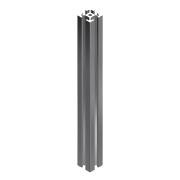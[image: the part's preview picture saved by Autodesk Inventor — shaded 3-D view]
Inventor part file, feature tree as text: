
AUTODESK INVENTOR PART (.ipt)
format: ipt  version: 2018 (Build 220112000, 112)  size: 148,480 bytes
history: native  units: mm
features: extrude x1, sketch x1
ambient origin geometry x8: Origin, YZ Plane, XZ Plane, XY Plane, X Axis, Y Axis, Z Axis, Center Point
bodies: Solid1 (feature_tree)
feature tree (2):
  extrude  "Extrusion1"  [1 undecoded]
  sketch  "Sketch1"  dims[d0=200.0mm d1=0.0mm]
note: 1 required parameter value undecoded (feature->parameter linkage not recoverable at this tier; creation-order binding heuristic only, values carry confidence <= 0.55)
